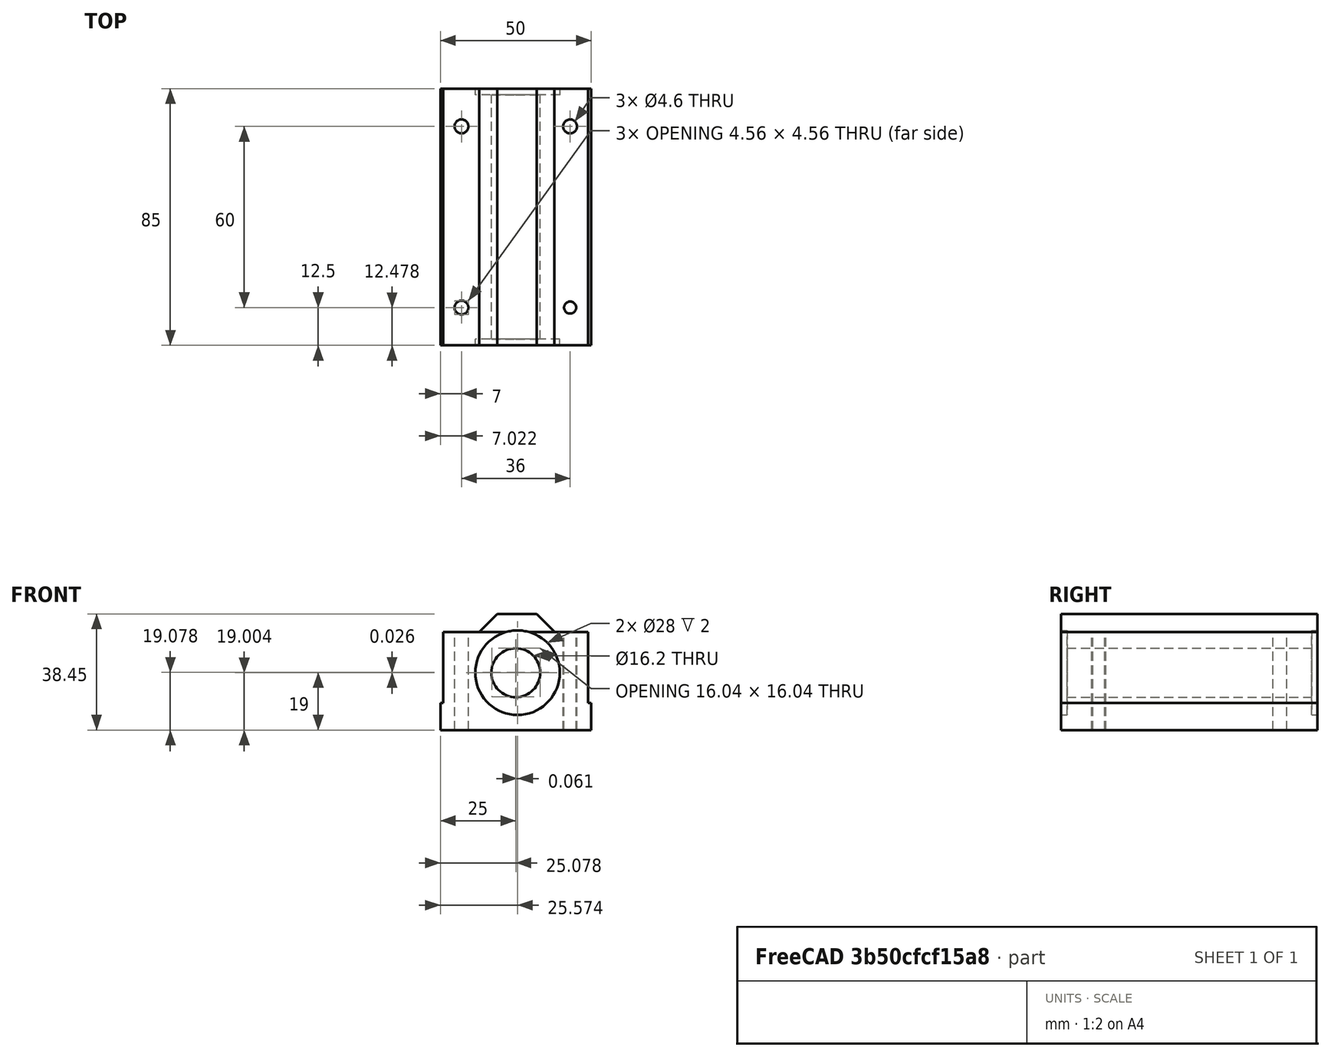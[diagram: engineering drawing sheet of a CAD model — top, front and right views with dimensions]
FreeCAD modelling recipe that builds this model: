
FCSTD DOCUMENT
Label: sc16wuu
objects: Part::Cut×12, Part::Cylinder×7, Part::Box×6, Part::MultiFuse×1
note: 26 computed .brp shape members not serialized (recipe doc carries the construction recipe); baked Part::Feature solids carry a one-line shape summary decoded from their .brp

FEATURE [Part::Box] Box
  Height = 32.5
  Length = 50
  Width = 85
FEATURE [Part::Cylinder] Cylinder
  Angle = 360
  Height = 100
  Placement = pos=(25,-4.78696,19) rot=(-1,0,0;1.5708rad)
  Radius = 8.1
FEATURE [Part::Cut] Cut
  Base = -> Box
  Tool = -> Cylinder
FEATURE [Part::Box] Box001
  Height = 6
  Length = 25
  Placement = pos=(-43.8255,-3.33042e-05,2.24746) rot=(0,0,1;0rad)
  Width = 85
FEATURE [Part::Box] Box002
  Height = 10
  Length = 10
  Placement = pos=(-50.8986,-3,9.31859) rot=(0,1,0;0.785397rad)
  Width = 90
FEATURE [Part::Cut] Cut001
  Base = -> Box001
  Tool = -> Box002
FEATURE [Part::Box] Box003
  Height = 10
  Length = 10
  Placement = pos=(-18.82,-2,2.25) rot=(0,-1,0;0.785397rad)
  Width = 90
FEATURE [Part::Cut] Cut002
  Base = -> Cut001
  Placement = pos=(56.6969,-0.000184233,30.2) rot=(0,0,1;0rad)
  Tool = -> Box003
FEATURE [Part::MultiFuse] Fusion
  Shapes = -> [Cut,Cut002]
FEATURE [Part::Box] Box004
  Height = 23.5
  Length = 1
  Placement = pos=(0,0,9) rot=(0,0,1;0rad)
  Width = 85
FEATURE [Part::Cut] Cut003
  Base = -> Fusion
  Tool = -> Box004
FEATURE [Part::Box] Box005
  Height = 23.5
  Length = 1
  Placement = pos=(49,0,9) rot=(0,0,1;0rad)
  Width = 85
FEATURE [Part::Cut] Cut004
  Base = -> Cut003
  Tool = -> Box005
FEATURE [Part::Cylinder] Cylinder001
  Angle = 360
  Height = 40
  Placement = pos=(7,12.5,-2) rot=(0,0,1;0rad)
  Radius = 2.3
FEATURE [Part::Cut] Cut005
  Base = -> Cut004
  Tool = -> Cylinder001
FEATURE [Part::Cylinder] Cylinder002
  Angle = 360
  Height = 40
  Placement = pos=(7,72.5,-3) rot=(0,0,1;0rad)
  Radius = 2.3
FEATURE [Part::Cut] Cut006
  Base = -> Cut005
  Tool = -> Cylinder002
FEATURE [Part::Cylinder] Cylinder003
  Angle = 360
  Height = 40
  Placement = pos=(43,12.5,-4) rot=(0,0,1;0rad)
  Radius = 2
FEATURE [Part::Cut] Cut007
  Base = -> Cut006
  Tool = -> Cylinder003
FEATURE [Part::Cylinder] Cylinder004
  Angle = 360
  Height = 40
  Placement = pos=(43,72.5,-4) rot=(0,0,1;0rad)
  Radius = 2.3
FEATURE [Part::Cut] Cut008
  Base = -> Cut007
  Tool = -> Cylinder004
FEATURE [Part::Cylinder] Cylinder005
  Angle = 360
  Height = 3
  Placement = pos=(25.5737,-1,19.0038) rot=(-1,0,0;1.5708rad)
  Radius = 14
FEATURE [Part::Cut] Cut009
  Base = -> Cut008
  Tool = -> Cylinder005
FEATURE [Part::Cut] Cut010
  Base = -> Cut009
  Tool = -> Cylinder005
FEATURE [Part::Cylinder] Cylinder006
  Angle = 360
  Height = 3
  Placement = pos=(25.6346,83,19.0294) rot=(-1,0,0;1.5708rad)
  Radius = 14
FEATURE [Part::Cut] Cut011
  Base = -> Cut010
  Tool = -> Cylinder006
